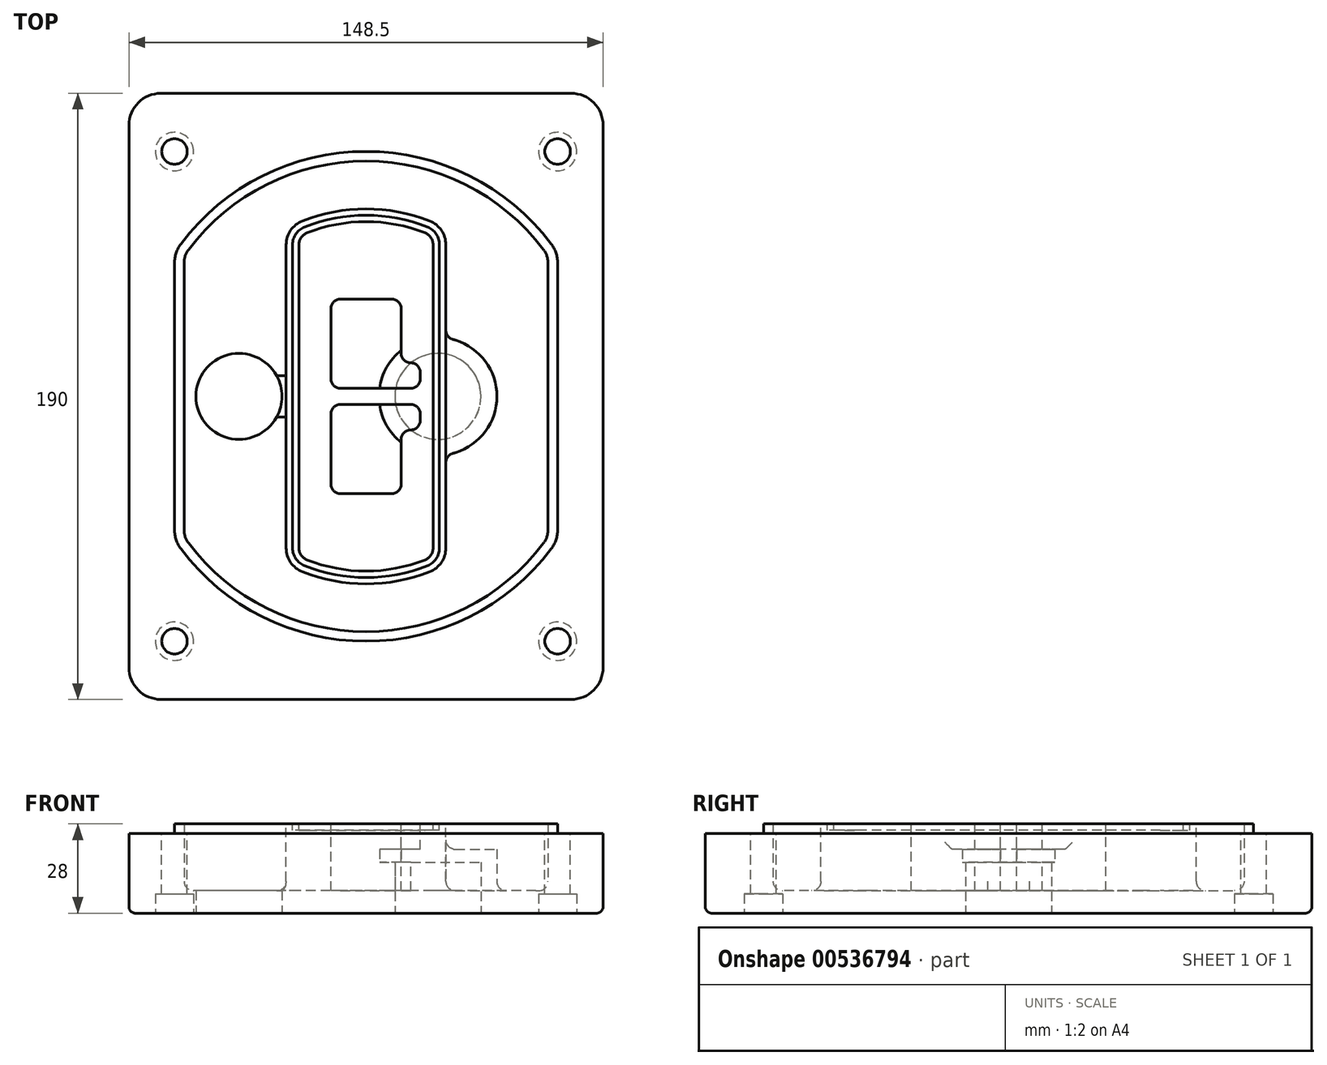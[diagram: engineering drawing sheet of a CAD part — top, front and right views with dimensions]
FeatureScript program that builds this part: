
annotation { "Feature Type Name" : "Feature", "Feature Type Description" : "" }
export const myFeature = defineFeature(function(context is Context, id is Id, definition is map)
    precondition{}
    {
        {
            var Q0;
            Q0=qCreatedBy(makeId("Top.planeOp"),FACE);
            var sketch = newSketch(context, id + "F0", { "sketchPlane" : qUnion([Q0])});
            skPoint(sketch, "E0.rect.middle", {"position": v(0, 0) * mm});
            skLineSegment(sketch, "E1.bottom", {"start": v(-64.25, -95) * mm, "end": v(64.25, -95) * mm});
            skLineSegment(sketch, "E1.top", {"start": v(-64.25, 95) * mm, "end": v(64.25, 95) * mm});
            skLineSegment(sketch, "E1.left", {"start": v(-74.25, -85) * mm, "end": v(-74.25, 85) * mm});
            skLineSegment(sketch, "E1.right", {"start": v(74.25, -85) * mm, "end": v(74.25, 85) * mm});
            skLineSegment(sketch, "E2", {"start": v(-74.25, 95) * mm, "end": v(74.25, -95) * mm, "construction": true});
            skLineSegment(sketch, "E3", {"start": v(74.25, 95) * mm, "end": v(-74.25, -95) * mm, "construction": true});
            skCircle(sketch, "E4", {"center": v(-60, 76.77) * mm, "radius": 4 * mm});
            skCircle(sketch, "E5", {"center": v(60, 76.77) * mm, "radius": 4 * mm});
            skCircle(sketch, "E6", {"center": v(60, -76.77) * mm, "radius": 4 * mm});
            skCircle(sketch, "E7", {"center": v(-60, -76.77) * mm, "radius": 4 * mm});
            skLineSegment(sketch, "E8", {"start": v(-60, 76.77) * mm, "end": v(60, 76.77) * mm, "construction": true});
            skLineSegment(sketch, "E9", {"start": v(60, 76.77) * mm, "end": v(60, -76.77) * mm, "construction": true});
            skLineSegment(sketch, "E10", {"start": v(60, -76.77) * mm, "end": v(-60, -76.77) * mm, "construction": true});
            skLineSegment(sketch, "E11", {"start": v(-60, -76.77) * mm, "end": v(-60, 76.77) * mm, "construction": true});
            skLineSegment(sketch, "E12", {"start": v(-60, 41.8) * mm, "end": v(-60, -41.8) * mm});
            skLineSegment(sketch, "E13", {"start": v(60, 41.8) * mm, "end": v(60, -41.8) * mm});
            skArc(sketch, "E14", {"start": v(58, 47.8) * mm, "mid": v(0, 76.77) * mm, "end": v(-58, 47.8) * mm});
            skArc(sketch, "E15", {"start": v(-58, -47.8) * mm, "mid": v(0, -76.77) * mm, "end": v(58, -47.8) * mm});
            skLineSegment(sketch, "E16", {"start": v(-60, 0) * mm, "end": v(60, 0) * mm, "construction": true});
            skPoint(sketch, "E17.visualSharp", {"position": v(-60, -45) * mm});
            skArc(sketch, "E17.filletArc", {"start": v(-60, -41.8) * mm, "mid": v(-59.49, -44.96) * mm, "end": v(-58, -47.8) * mm});
            skPoint(sketch, "E18.visualSharp", {"position": v(-60, 45) * mm});
            skArc(sketch, "E18.filletArc", {"start": v(-58, 47.8) * mm, "mid": v(-59.49, 44.96) * mm, "end": v(-60, 41.8) * mm});
            skPoint(sketch, "E19.visualSharp", {"position": v(60, 45) * mm});
            skArc(sketch, "E19.filletArc", {"start": v(60, 41.8) * mm, "mid": v(59.49, 44.96) * mm, "end": v(58, 47.8) * mm});
            skPoint(sketch, "E20.visualSharp", {"position": v(60, -45) * mm});
            skArc(sketch, "E20.filletArc", {"start": v(58, -47.8) * mm, "mid": v(59.49, -44.96) * mm, "end": v(60, -41.8) * mm});
            skPoint(sketch, "E21.visualSharp", {"position": v(-74.25, 95) * mm});
            skArc(sketch, "E21.filletArc", {"start": v(-64.25, 95) * mm, "mid": v(-71.32, 92.07) * mm, "end": v(-74.25, 85) * mm});
            skPoint(sketch, "E22.visualSharp", {"position": v(74.25, 95) * mm});
            skArc(sketch, "E22.filletArc", {"start": v(74.25, 85) * mm, "mid": v(71.32, 92.07) * mm, "end": v(64.25, 95) * mm});
            skPoint(sketch, "E23.visualSharp", {"position": v(74.25, -95) * mm});
            skArc(sketch, "E23.filletArc", {"start": v(64.25, -95) * mm, "mid": v(71.32, -92.07) * mm, "end": v(74.25, -85) * mm});
            skPoint(sketch, "E24.visualSharp", {"position": v(-74.25, -95) * mm});
            skArc(sketch, "E24.filletArc", {"start": v(-74.25, -85) * mm, "mid": v(-71.32, -92.07) * mm, "end": v(-64.25, -95) * mm});
            skArc(sketch, "E25.0", {"start": v(57, 41.8) * mm, "mid": v(56.64, 44.01) * mm, "end": v(55.6, 46) * mm});
            skLineSegment(sketch, "E25.1", {"start": v(57, 41.8) * mm, "end": v(57, -41.8) * mm});
            skArc(sketch, "E25.2", {"start": v(55.6, -46) * mm, "mid": v(56.64, -44.01) * mm, "end": v(57, -41.8) * mm});
            skArc(sketch, "E25.3", {"start": v(-55.6, -46) * mm, "mid": v(0, -73.77) * mm, "end": v(55.6, -46) * mm});
            skArc(sketch, "E25.4", {"start": v(-57, -41.8) * mm, "mid": v(-56.64, -44.01) * mm, "end": v(-55.6, -46) * mm});
            skArc(sketch, "E25.5", {"start": v(55.6, 46) * mm, "mid": v(0, 73.77) * mm, "end": v(-55.6, 46) * mm});
            skLineSegment(sketch, "E25.6", {"start": v(-57, 41.8) * mm, "end": v(-57, -41.8) * mm});
            skArc(sketch, "E25.7", {"start": v(-55.6, 46) * mm, "mid": v(-56.64, 44.01) * mm, "end": v(-57, 41.8) * mm});
            skArc(sketch, "E26.0", {"start": v(-61.2, 50.2) * mm, "mid": v(-63.28, 46.23) * mm, "end": v(-64, 41.8) * mm});
            skArc(sketch, "E26.1", {"start": v(61.2, 50.2) * mm, "mid": v(0, 80.77) * mm, "end": v(-61.2, 50.2) * mm});
            skArc(sketch, "E26.2", {"start": v(64, 41.8) * mm, "mid": v(63.28, 46.23) * mm, "end": v(61.2, 50.2) * mm});
            skLineSegment(sketch, "E26.3", {"start": v(64, 41.8) * mm, "end": v(64, -41.8) * mm});
            skArc(sketch, "E26.4", {"start": v(61.2, -50.2) * mm, "mid": v(63.28, -46.23) * mm, "end": v(64, -41.8) * mm});
            skLineSegment(sketch, "E26.5", {"start": v(-64, 41.8) * mm, "end": v(-64, -41.8) * mm});
            skArc(sketch, "E26.6", {"start": v(-61.2, -50.2) * mm, "mid": v(0, -80.77) * mm, "end": v(61.2, -50.2) * mm});
            skArc(sketch, "E26.7", {"start": v(-64, -41.8) * mm, "mid": v(-63.28, -46.23) * mm, "end": v(-61.2, -50.2) * mm});
            skSolve(sketch);
        }
        {
            var Q0;
            Q0=makeQuery(id+"F0.imprint","IMPRINT",FACE,{"disambiguationData":[TD([[makeQuery(id+"F0.imprint","IMPRINT",EDGE,{"derivedFrom":sQuery(id+"F0.wireOp",EDGE,"E1.bottom")}),1.0]])]});
            var Q1;
            Q1=makeQuery(id+"F0.imprint","IMPRINT",FACE,{"disambiguationData":[TD([[makeQuery(id+"F0.imprint","IMPRINT",EDGE,{"derivedFrom":sQuery(id+"F0.wireOp",EDGE,"E12")}),1.0]])]});
            var Q2;
            Q2=makeQuery(id+"F0.imprint","IMPRINT",FACE,{"disambiguationData":[TD([[makeQuery(id+"F0.imprint","IMPRINT",EDGE,{"derivedFrom":sQuery(id+"F0.wireOp",EDGE,"E25.0")}),1.0]])]});
            var Q3;
            Q3=makeQuery(id+"F0.imprint","IMPRINT",FACE,{"disambiguationData":[TD([[makeQuery(id+"F0.imprint","IMPRINT",EDGE,{"derivedFrom":sQuery(id+"F0.wireOp",EDGE,"E12")}),-1.0]])]});
            extrude(context, id + "F1", {"entities" : qUnion([Q0, Q1, Q2, Q3]), "oppositeDirection" : true, "depth" : 25 * mm, "offsetDistance" : 25 * mm});
        }
        {
            var Q0;
            Q0=makeQuery(id+"F0.imprint","IMPRINT",FACE,{"disambiguationData":[TD([[makeQuery(id+"F0.imprint","IMPRINT",EDGE,{"derivedFrom":sQuery(id+"F0.wireOp",EDGE,"E12")}),1.0]])]});
            extrude(context, id + "F2", {"entities" : qUnion([Q0]), "operationType" : NewBodyOperationType.ADD, "depth" : 3 * mm});
        }
        {
            var Q0;
            Q0=makeQuery(id+"F0.imprint","IMPRINT",FACE,{"disambiguationData":[TD([[makeQuery(id+"F0.imprint","IMPRINT",EDGE,{"derivedFrom":sQuery(id+"F0.wireOp",EDGE,"E25.0")}),1.0]])]});
            extrude(context, id + "F3", {"entities" : qUnion([Q0]), "operationType" : NewBodyOperationType.REMOVE, "oppositeDirection" : true, "depth" : 18 * mm});
        }
        {
            var Q0;
            Q0=makeQuery(id+"F2.opExtrude","CAP_FACE",FACE,{"disambiguationData":[OSD([sQuery(id+"F0.wireOp",EDGE,"E12"),sQuery(id+"F0.wireOp",EDGE,"E13"),sQuery(id+"F0.wireOp",EDGE,"E14"),sQuery(id+"F0.wireOp",EDGE,"E15"),sQuery(id+"F0.wireOp",EDGE,"E17.filletArc"),sQuery(id+"F0.wireOp",EDGE,"E18.filletArc"),sQuery(id+"F0.wireOp",EDGE,"E19.filletArc"),sQuery(id+"F0.wireOp",EDGE,"E20.filletArc"),sQuery(id+"F0.wireOp",EDGE,"E25.0"),sQuery(id+"F0.wireOp",EDGE,"E25.1"),sQuery(id+"F0.wireOp",EDGE,"E25.2"),sQuery(id+"F0.wireOp",EDGE,"E25.3"),sQuery(id+"F0.wireOp",EDGE,"E25.4"),sQuery(id+"F0.wireOp",EDGE,"E25.5"),sQuery(id+"F0.wireOp",EDGE,"E25.6"),sQuery(id+"F0.wireOp",EDGE,"E25.7")])],"isStart":false});
            var sketch = newSketch(context, id + "F4", { "sketchPlane" : qUnion([Q0])});
            skArc(sketch, "E27.0", {"start": v(-19.92, -55) * mm, "mid": v(0, -58.77) * mm, "end": v(19.92, -55) * mm});
            skArc(sketch, "E28.0", {"start": v(19.92, 55) * mm, "mid": v(0, 58.77) * mm, "end": v(-19.92, 55) * mm});
            skLineSegment(sketch, "E29", {"start": v(-25, 47.55) * mm, "end": v(-25, -47.55) * mm});
            skLineSegment(sketch, "E30", {"start": v(25, 47.55) * mm, "end": v(25, -47.55) * mm});
            skLineSegment(sketch, "E31", {"start": v(-25, 52.7) * mm, "end": v(25, 52.7) * mm, "construction": true});
            skLineSegment(sketch, "E32", {"start": v(-25, -52.7) * mm, "end": v(25, -52.7) * mm, "construction": true});
            skPoint(sketch, "E33.visualSharp", {"position": v(-25, 52.7) * mm});
            skArc(sketch, "E33.filletArc", {"start": v(-19.92, 55) * mm, "mid": v(-23.6, 52.06) * mm, "end": v(-25, 47.55) * mm});
            skPoint(sketch, "E34.visualSharp", {"position": v(25, 52.7) * mm});
            skArc(sketch, "E34.filletArc", {"start": v(25, 47.55) * mm, "mid": v(23.6, 52.06) * mm, "end": v(19.92, 55) * mm});
            skPoint(sketch, "E35.visualSharp", {"position": v(25, -52.7) * mm});
            skArc(sketch, "E35.filletArc", {"start": v(19.92, -55) * mm, "mid": v(23.6, -52.06) * mm, "end": v(25, -47.55) * mm});
            skPoint(sketch, "E36.visualSharp", {"position": v(-25, -52.7) * mm});
            skArc(sketch, "E36.filletArc", {"start": v(-25, -47.55) * mm, "mid": v(-23.6, -52.06) * mm, "end": v(-19.92, -55) * mm});
            skArc(sketch, "E37.0", {"start": v(55.6, 46) * mm, "mid": v(0, 73.77) * mm, "end": v(-55.6, 46) * mm});
            skArc(sketch, "E37.1", {"start": v(-55.6, 46) * mm, "mid": v(-56.64, 44.01) * mm, "end": v(-57, 41.8) * mm});
            skLineSegment(sketch, "E37.2", {"start": v(-57, 41.8) * mm, "end": v(-57, -41.8) * mm});
            skArc(sketch, "E37.3", {"start": v(-57, -41.8) * mm, "mid": v(-56.64, -44.01) * mm, "end": v(-55.6, -46) * mm});
            skArc(sketch, "E37.4", {"start": v(-55.6, -46) * mm, "mid": v(0, -73.77) * mm, "end": v(55.6, -46) * mm});
            skArc(sketch, "E37.5", {"start": v(55.6, -46) * mm, "mid": v(56.64, -44.01) * mm, "end": v(57, -41.8) * mm});
            skLineSegment(sketch, "E37.6", {"start": v(57, 41.8) * mm, "end": v(57, -41.8) * mm});
            skArc(sketch, "E37.7", {"start": v(57, 41.8) * mm, "mid": v(56.64, 44.01) * mm, "end": v(55.6, 46) * mm});
            skLineSegment(sketch, "E38.0", {"start": v(23, 47.55) * mm, "end": v(23, -47.55) * mm});
            skArc(sketch, "E38.1", {"start": v(19.2, -53.14) * mm, "mid": v(21.96, -50.93) * mm, "end": v(23, -47.55) * mm});
            skArc(sketch, "E38.2", {"start": v(-19.2, -53.14) * mm, "mid": v(0, -56.77) * mm, "end": v(19.2, -53.14) * mm});
            skArc(sketch, "E38.3", {"start": v(-23, -47.55) * mm, "mid": v(-21.96, -50.93) * mm, "end": v(-19.2, -53.14) * mm});
            skLineSegment(sketch, "E38.4", {"start": v(-23, 47.55) * mm, "end": v(-23, -47.55) * mm});
            skArc(sketch, "E38.5", {"start": v(23, 47.55) * mm, "mid": v(21.96, 50.93) * mm, "end": v(19.2, 53.14) * mm});
            skArc(sketch, "E38.6", {"start": v(-19.2, 53.14) * mm, "mid": v(-21.96, 50.93) * mm, "end": v(-23, 47.55) * mm});
            skArc(sketch, "E38.7", {"start": v(19.2, 53.14) * mm, "mid": v(0, 56.77) * mm, "end": v(-19.2, 53.14) * mm});
            skArc(sketch, "E39.0", {"start": v(21, 47.55) * mm, "mid": v(20.3, 49.8) * mm, "end": v(18.46, 51.28) * mm});
            skLineSegment(sketch, "E39.1", {"start": v(21, 47.55) * mm, "end": v(21, -47.55) * mm});
            skArc(sketch, "E39.2", {"start": v(18.46, -51.28) * mm, "mid": v(20.3, -49.8) * mm, "end": v(21, -47.55) * mm});
            skArc(sketch, "E39.3", {"start": v(-18.46, -51.28) * mm, "mid": v(0, -54.77) * mm, "end": v(18.46, -51.28) * mm});
            skArc(sketch, "E39.4", {"start": v(-21, -47.55) * mm, "mid": v(-20.3, -49.8) * mm, "end": v(-18.46, -51.28) * mm});
            skArc(sketch, "E39.5", {"start": v(18.46, 51.28) * mm, "mid": v(0, 54.77) * mm, "end": v(-18.46, 51.28) * mm});
            skLineSegment(sketch, "E39.6", {"start": v(-21, 47.55) * mm, "end": v(-21, -47.55) * mm});
            skArc(sketch, "E39.7", {"start": v(-18.46, 51.28) * mm, "mid": v(-20.3, 49.8) * mm, "end": v(-21, 47.55) * mm});
            skLineSegment(sketch, "E40", {"start": v(-25, 0) * mm, "end": v(25, 0) * mm, "construction": true});
            skLineSegment(sketch, "E41", {"start": v(-11, 5.5) * mm, "end": v(-11, 27.5) * mm});
            skLineSegment(sketch, "E42", {"start": v(-8, 30.5) * mm, "end": v(8, 30.5) * mm});
            skLineSegment(sketch, "E43", {"start": v(11, 27.5) * mm, "end": v(11, 13.5) * mm});
            skLineSegment(sketch, "E44", {"start": v(14, 10.5) * mm, "end": v(14, 10.5) * mm});
            skLineSegment(sketch, "E45", {"start": v(17, 7.5) * mm, "end": v(17, 5.5) * mm});
            skLineSegment(sketch, "E46", {"start": v(14, 2.5) * mm, "end": v(-8, 2.5) * mm});
            skPoint(sketch, "E47.visualSharp", {"position": v(-11, 30.5) * mm});
            skArc(sketch, "E47.filletArc", {"start": v(-8, 30.5) * mm, "mid": v(-10.12, 29.62) * mm, "end": v(-11, 27.5) * mm});
            skPoint(sketch, "E48.visualSharp", {"position": v(11, 30.5) * mm});
            skArc(sketch, "E48.filletArc", {"start": v(11, 27.5) * mm, "mid": v(10.12, 29.62) * mm, "end": v(8, 30.5) * mm});
            skPoint(sketch, "E49.visualSharp", {"position": v(11, 10.5) * mm});
            skArc(sketch, "E49.filletArc", {"start": v(11, 13.5) * mm, "mid": v(11.88, 11.38) * mm, "end": v(14, 10.5) * mm});
            skPoint(sketch, "E50.visualSharp", {"position": v(17, 10.5) * mm});
            skArc(sketch, "E50.filletArc", {"start": v(17, 7.5) * mm, "mid": v(16.12, 9.62) * mm, "end": v(14, 10.5) * mm});
            skPoint(sketch, "E51.visualSharp", {"position": v(17, 2.5) * mm});
            skArc(sketch, "E51.filletArc", {"start": v(14, 2.5) * mm, "mid": v(16.12, 3.38) * mm, "end": v(17, 5.5) * mm});
            skPoint(sketch, "E52.visualSharp", {"position": v(-11, 2.5) * mm});
            skArc(sketch, "E52.filletArc", {"start": v(-11, 5.5) * mm, "mid": v(-10.12, 3.38) * mm, "end": v(-8, 2.5) * mm});
            skLineSegment(sketch, "E53.0.MirrorCS", {"start": v(14, -2.5) * mm, "end": v(-8, -2.5) * mm});
            skArc(sketch, "E54.0.MirrorCS", {"start": v(-11, -5.5) * mm, "mid": v(-10.12, -3.38) * mm, "end": v(-8, -2.5) * mm});
            skLineSegment(sketch, "E55.0.MirrorCS", {"start": v(-11, -5.5) * mm, "end": v(-11, -27.5) * mm});
            skArc(sketch, "E56.0.MirrorCS", {"start": v(-8, -30.5) * mm, "mid": v(-10.12, -29.62) * mm, "end": v(-11, -27.5) * mm});
            skLineSegment(sketch, "E57.0.MirrorCS", {"start": v(-8, -30.5) * mm, "end": v(8, -30.5) * mm});
            skArc(sketch, "E58.0.MirrorCS", {"start": v(11, -27.5) * mm, "mid": v(10.12, -29.62) * mm, "end": v(8, -30.5) * mm});
            skLineSegment(sketch, "E59.0.MirrorCS", {"start": v(11, -27.5) * mm, "end": v(11, -13.5) * mm});
            skArc(sketch, "E60.0.MirrorCS", {"start": v(11, -13.5) * mm, "mid": v(11.88, -11.38) * mm, "end": v(14, -10.5) * mm});
            skArc(sketch, "E61.0.MirrorCS", {"start": v(17, -7.5) * mm, "mid": v(16.12, -9.62) * mm, "end": v(14, -10.5) * mm});
            skLineSegment(sketch, "E62.0.MirrorCS", {"start": v(17, -7.5) * mm, "end": v(17, -5.5) * mm});
            skArc(sketch, "E63.0.MirrorCS", {"start": v(14, -2.5) * mm, "mid": v(16.12, -3.38) * mm, "end": v(17, -5.5) * mm});
            skSolve(sketch);
        }
        {
            var Q0;
            Q0=makeQuery(id+"F4.imprint","IMPRINT",FACE,{"disambiguationData":[TD([[makeQuery(id+"F4.imprint","IMPRINT",EDGE,{"derivedFrom":sQuery(id+"F4.wireOp",EDGE,"E27.0")}),1.0]])]});
            var Q1;
            Q1=makeQuery(id+"F4.imprint","IMPRINT",FACE,{"disambiguationData":[TD([[makeQuery(id+"F4.imprint","IMPRINT",EDGE,{"derivedFrom":sQuery(id+"F4.wireOp",EDGE,"E38.0")}),-1.0]])]});
            var Q2;
            Q2=makeQuery(id+"F4.imprint","IMPRINT",FACE,{"disambiguationData":[TD([[makeQuery(id+"F4.imprint","IMPRINT",EDGE,{"derivedFrom":sQuery(id+"F4.wireOp",EDGE,"E39.0")}),1.0]])]});
            extrude(context, id + "F5", {"entities" : qUnion([Q0, Q1, Q2]), "operationType" : NewBodyOperationType.ADD, "endBound" : BoundingType.UP_TO_NEXT, "oppositeDirection" : true, "depth" : 25 * mm});
        }
        {
            var Q0;
            Q0=makeQuery(id+"F4.imprint","IMPRINT",FACE,{"disambiguationData":[TD([[makeQuery(id+"F4.imprint","IMPRINT",EDGE,{"derivedFrom":sQuery(id+"F4.wireOp",EDGE,"E38.0")}),-1.0]])]});
            extrude(context, id + "F6", {"entities" : qUnion([Q0]), "operationType" : NewBodyOperationType.REMOVE, "oppositeDirection" : true, "depth" : 2 * mm});
        }
        {
            var Q0;
            Q0=makeQuery(id+"F1.opExtrude","CAP_FACE",FACE,{"disambiguationData":[OSD([sQuery(id+"F0.wireOp",EDGE,"E1.bottom"),sQuery(id+"F0.wireOp",EDGE,"E1.top"),sQuery(id+"F0.wireOp",EDGE,"E1.left"),sQuery(id+"F0.wireOp",EDGE,"E1.right"),sQuery(id+"F0.wireOp",EDGE,"E4"),sQuery(id+"F0.wireOp",EDGE,"E5"),sQuery(id+"F0.wireOp",EDGE,"E6"),sQuery(id+"F0.wireOp",EDGE,"E7"),sQuery(id+"F0.wireOp",EDGE,"E21.filletArc"),sQuery(id+"F0.wireOp",EDGE,"E22.filletArc"),sQuery(id+"F0.wireOp",EDGE,"E23.filletArc"),sQuery(id+"F0.wireOp",EDGE,"E24.filletArc")])],"isStart":false});
            var sketch = newSketch(context, id + "F7", { "sketchPlane" : qUnion([Q0])});
            skCircle(sketch, "E64", {"center": v(22.5, 0) * mm, "radius": 13.47 * mm});
            skCircle(sketch, "E65", {"center": v(-39.81, 0) * mm, "radius": 13.47 * mm});
            skLineSegment(sketch, "E66", {"start": v(74.25, 0) * mm, "end": v(-74.25, 0) * mm});
            skCircle(sketch, "E67", {"center": v(22.5, 0) * mm, "radius": 18.47 * mm});
            skCircle(sketch, "E68", {"center": v(60, -76.77) * mm, "radius": 6 * mm});
            skCircle(sketch, "E69", {"center": v(-60, -76.77) * mm, "radius": 6 * mm});
            skCircle(sketch, "E70", {"center": v(-60, 76.77) * mm, "radius": 6 * mm});
            skCircle(sketch, "E71", {"center": v(60, 76.77) * mm, "radius": 6 * mm});
            skSolve(sketch);
        }
        {
            var Q0;
            {var subQ1=sQuery(id+"F7.wireOp",EDGE,"E66");var subQ4=sQuery(id+"F7.wireOp",EDGE,"E64");var subQ6=makeQuery(id+"F7.imprint","INTERSECT",VERTEX,{"disambiguationData":[OD(0.0)],"derivedFrom":[subQ4,subQ1]});Q0=makeQuery(id+"F7.imprint","IMPRINT",FACE,{"disambiguationData":[TD([[makeQuery(id+"F7.imprint","IMPRINT",EDGE,{"disambiguationData":[TD([[subQ6,-1.0]])],"derivedFrom":subQ4}),-1.0]])]});}
            var Q1;
            {var subQ0=sQuery(id+"F7.wireOp",EDGE,"E66");var subQ1=sQuery(id+"F7.wireOp",EDGE,"E64");var subQ3=makeQuery(id+"F7.imprint","INTERSECT",VERTEX,{"disambiguationData":[OD(0.0)],"derivedFrom":[subQ1,subQ0]});Q1=makeQuery(id+"F7.imprint","IMPRINT",FACE,{"disambiguationData":[TD([[makeQuery(id+"F7.imprint","IMPRINT",EDGE,{"disambiguationData":[TD([[subQ3,-1.0]])],"derivedFrom":subQ1}),1.0]])]});}
            var Q2;
            {var subQ0=sQuery(id+"F7.wireOp",EDGE,"E66");var subQ1=sQuery(id+"F7.wireOp",EDGE,"E64");var subQ3=makeQuery(id+"F7.imprint","INTERSECT",VERTEX,{"disambiguationData":[OD(0.0)],"derivedFrom":[subQ1,subQ0]});Q2=makeQuery(id+"F7.imprint","IMPRINT",FACE,{"disambiguationData":[TD([[makeQuery(id+"F7.imprint","IMPRINT",EDGE,{"disambiguationData":[TD([[subQ3,1.0]])],"derivedFrom":subQ1}),1.0]])]});}
            var Q3;
            {var subQ1=sQuery(id+"F7.wireOp",EDGE,"E66");var subQ4=sQuery(id+"F7.wireOp",EDGE,"E64");var subQ6=makeQuery(id+"F7.imprint","INTERSECT",VERTEX,{"disambiguationData":[OD(0.0)],"derivedFrom":[subQ4,subQ1]});Q3=makeQuery(id+"F7.imprint","IMPRINT",FACE,{"disambiguationData":[TD([[makeQuery(id+"F7.imprint","IMPRINT",EDGE,{"disambiguationData":[TD([[subQ6,1.0]])],"derivedFrom":subQ4}),-1.0]])]});}
            extrude(context, id + "F8", {"entities" : qUnion([Q0, Q1, Q2, Q3]), "operationType" : NewBodyOperationType.ADD, "oppositeDirection" : true, "depth" : 20 * mm});
        }
        {
            var Q0;
            {var subQ0=sQuery(id+"F7.wireOp",EDGE,"E66");var subQ1=sQuery(id+"F7.wireOp",EDGE,"E64");var subQ3=makeQuery(id+"F7.imprint","INTERSECT",VERTEX,{"disambiguationData":[OD(0.0)],"derivedFrom":[subQ1,subQ0]});Q0=makeQuery(id+"F7.imprint","IMPRINT",FACE,{"disambiguationData":[TD([[makeQuery(id+"F7.imprint","IMPRINT",EDGE,{"disambiguationData":[TD([[subQ3,-1.0]])],"derivedFrom":subQ1}),1.0]])]});}
            var Q1;
            {var subQ0=sQuery(id+"F7.wireOp",EDGE,"E66");var subQ1=sQuery(id+"F7.wireOp",EDGE,"E64");var subQ3=makeQuery(id+"F7.imprint","INTERSECT",VERTEX,{"disambiguationData":[OD(0.0)],"derivedFrom":[subQ1,subQ0]});Q1=makeQuery(id+"F7.imprint","IMPRINT",FACE,{"disambiguationData":[TD([[makeQuery(id+"F7.imprint","IMPRINT",EDGE,{"disambiguationData":[TD([[subQ3,1.0]])],"derivedFrom":subQ1}),1.0]])]});}
            extrude(context, id + "F9", {"entities" : qUnion([Q0, Q1]), "operationType" : NewBodyOperationType.REMOVE, "oppositeDirection" : true, "depth" : 16 * mm});
        }
        {
            var Q0;
            {var subQ0=sQuery(id+"F7.wireOp",EDGE,"E66");var subQ1=sQuery(id+"F7.wireOp",EDGE,"E65");var subQ3=makeQuery(id+"F7.imprint","INTERSECT",VERTEX,{"disambiguationData":[OD(0.0)],"derivedFrom":[subQ1,subQ0]});Q0=makeQuery(id+"F7.imprint","IMPRINT",FACE,{"disambiguationData":[TD([[makeQuery(id+"F7.imprint","IMPRINT",EDGE,{"disambiguationData":[TD([[subQ3,-1.0]])],"derivedFrom":subQ1}),1.0]])]});}
            var Q1;
            {var subQ0=sQuery(id+"F7.wireOp",EDGE,"E66");var subQ1=sQuery(id+"F7.wireOp",EDGE,"E65");var subQ3=makeQuery(id+"F7.imprint","INTERSECT",VERTEX,{"disambiguationData":[OD(0.0)],"derivedFrom":[subQ1,subQ0]});Q1=makeQuery(id+"F7.imprint","IMPRINT",FACE,{"disambiguationData":[TD([[makeQuery(id+"F7.imprint","IMPRINT",EDGE,{"disambiguationData":[TD([[subQ3,1.0]])],"derivedFrom":subQ1}),1.0]])]});}
            extrude(context, id + "F10", {"entities" : qUnion([Q0, Q1]), "operationType" : NewBodyOperationType.REMOVE, "oppositeDirection" : true, "depth" : 25 * mm});
        }
        {
            var Q0;
            Q0=makeQuery(id+"F7.imprint","IMPRINT",FACE,{"disambiguationData":[TD([[makeQuery(id+"F7.imprint","IMPRINT",EDGE,{"derivedFrom":sQuery(id+"F7.wireOp",EDGE,"E68")}),1.0]])]});
            var Q1;
            Q1=makeQuery(id+"F7.imprint","IMPRINT",FACE,{"disambiguationData":[TD([[makeQuery(id+"F7.imprint","IMPRINT",EDGE,{"derivedFrom":makeQuery(id+"F1.opExtrude","CAP_EDGE",EDGE,{"disambiguationData":[OSD([sQuery(id+"F0.wireOp",EDGE,"E5")])],"isStart":false})}),-1.0]])]});
            var Q2;
            Q2=makeQuery(id+"F7.imprint","IMPRINT",FACE,{"disambiguationData":[TD([[makeQuery(id+"F7.imprint","IMPRINT",EDGE,{"derivedFrom":sQuery(id+"F7.wireOp",EDGE,"E69")}),1.0]])]});
            var Q3;
            Q3=makeQuery(id+"F7.imprint","IMPRINT",FACE,{"disambiguationData":[TD([[makeQuery(id+"F7.imprint","IMPRINT",EDGE,{"derivedFrom":makeQuery(id+"F1.opExtrude","CAP_EDGE",EDGE,{"disambiguationData":[OSD([sQuery(id+"F0.wireOp",EDGE,"E4")])],"isStart":false})}),-1.0]])]});
            var Q4;
            Q4=makeQuery(id+"F7.imprint","IMPRINT",FACE,{"disambiguationData":[TD([[makeQuery(id+"F7.imprint","IMPRINT",EDGE,{"derivedFrom":sQuery(id+"F7.wireOp",EDGE,"E70")}),1.0]])]});
            var Q5;
            Q5=makeQuery(id+"F7.imprint","IMPRINT",FACE,{"disambiguationData":[TD([[makeQuery(id+"F7.imprint","IMPRINT",EDGE,{"derivedFrom":makeQuery(id+"F1.opExtrude","CAP_EDGE",EDGE,{"disambiguationData":[OSD([sQuery(id+"F0.wireOp",EDGE,"E7")])],"isStart":false})}),-1.0]])]});
            var Q6;
            Q6=makeQuery(id+"F7.imprint","IMPRINT",FACE,{"disambiguationData":[TD([[makeQuery(id+"F7.imprint","IMPRINT",EDGE,{"derivedFrom":sQuery(id+"F7.wireOp",EDGE,"E71")}),1.0]])]});
            var Q7;
            Q7=makeQuery(id+"F7.imprint","IMPRINT",FACE,{"disambiguationData":[TD([[makeQuery(id+"F7.imprint","IMPRINT",EDGE,{"derivedFrom":makeQuery(id+"F1.opExtrude","CAP_EDGE",EDGE,{"disambiguationData":[OSD([sQuery(id+"F0.wireOp",EDGE,"E6")])],"isStart":false})}),-1.0]])]});
            extrude(context, id + "F11", {"entities" : qUnion([Q0, Q1, Q2, Q3, Q4, Q5, Q6, Q7]), "operationType" : NewBodyOperationType.REMOVE, "oppositeDirection" : true, "depth" : 6 * mm});
        }
        {
            var Q0;
            Q0=makeQuery(id+"F9.boolean.opBoolean","COPY",FACE,{"derivedFrom":makeQuery(id+"F9.opExtrude","CAP_FACE",FACE,{"disambiguationData":[OSD([sQuery(id+"F7.wireOp",EDGE,"E64")])],"isStart":false})});
            var sketch = newSketch(context, id + "F12", { "sketchPlane" : qUnion([Q0])});
            skArc(sketch, "E72.0", {"start": v(11, 14.45) * mm, "mid": v(6.45, 9.13) * mm, "end": v(4.2, 2.5) * mm});
            skArc(sketch, "E72.1", {"start": v(4.2, -2.5) * mm, "mid": v(6.45, -9.13) * mm, "end": v(11, -14.45) * mm});
            skLineSegment(sketch, "E73", {"start": v(4.2, -2.5) * mm, "end": v(14, -2.5) * mm});
            skLineSegment(sketch, "E74.0", {"start": v(14, 2.5) * mm, "end": v(4.2, 2.5) * mm});
            skArc(sketch, "E74.1", {"start": v(14, 2.5) * mm, "mid": v(16.12, 3.38) * mm, "end": v(17, 5.5) * mm});
            skLineSegment(sketch, "E74.2", {"start": v(17, 7.5) * mm, "end": v(17, 5.5) * mm});
            skArc(sketch, "E74.3", {"start": v(17, 7.5) * mm, "mid": v(16.12, 9.62) * mm, "end": v(14, 10.5) * mm});
            skArc(sketch, "E74.4", {"start": v(11, 13.5) * mm, "mid": v(11.88, 11.38) * mm, "end": v(14, 10.5) * mm});
            skLineSegment(sketch, "E74.5", {"start": v(11, 14.45) * mm, "end": v(11, 13.5) * mm});
            skLineSegment(sketch, "E74.7", {"start": v(14, -2.5) * mm, "end": v(4.2, -2.5) * mm});
            skArc(sketch, "E74.8", {"start": v(14, -2.5) * mm, "mid": v(16.12, -3.38) * mm, "end": v(17, -5.5) * mm});
            skLineSegment(sketch, "E74.9", {"start": v(17, -7.5) * mm, "end": v(17, -5.5) * mm});
            skArc(sketch, "E74.10", {"start": v(17, -7.5) * mm, "mid": v(16.12, -9.62) * mm, "end": v(14, -10.5) * mm});
            skArc(sketch, "E74.11", {"start": v(11, -13.5) * mm, "mid": v(11.88, -11.38) * mm, "end": v(14, -10.5) * mm});
            skLineSegment(sketch, "E74.12", {"start": v(11, -14.45) * mm, "end": v(11, -13.5) * mm});
            skPoint(sketch, "E75.orphan", {"position": v(11, -27.5) * mm});
            skPoint(sketch, "E76.orphan", {"position": v(-8, -2.5) * mm});
            skPoint(sketch, "E77.orphan", {"position": v(-8, 2.5) * mm});
            skPoint(sketch, "E78.orphan", {"position": v(11, 27.5) * mm});
            skSolve(sketch);
        }
        {
            var Q0;
            {var subQ7=sQuery(id+"F12.wireOp",EDGE,"E72.0");var subQ14=sQuery(id+"F12.wireOp",EDGE,"E72.1");var subQ16=sQuery(id+"F12.wireOp",EDGE,"E74.1");var subQ18=sQuery(id+"F12.wireOp",EDGE,"E74.8");Q0=qUnion([makeQuery(id+"F12.imprint","IMPRINT",FACE,{"disambiguationData":[TD([[makeQuery(id+"F12.imprint","IMPRINT",EDGE,{"derivedFrom":subQ7}),1.0]])]}),makeQuery(id+"F12.imprint","IMPRINT",FACE,{"disambiguationData":[TD([[makeQuery(id+"F12.imprint","IMPRINT",EDGE,{"derivedFrom":subQ14}),1.0]])]}),makeQuery(id+"F12.imprint","IMPRINT",FACE,{"disambiguationData":[TD([[makeQuery(id+"F12.imprint","IMPRINT",EDGE,{"derivedFrom":subQ16}),1.0]])]}),makeQuery(id+"F12.imprint","IMPRINT",FACE,{"disambiguationData":[TD([[makeQuery(id+"F12.imprint","IMPRINT",EDGE,{"derivedFrom":subQ18}),-1.0]])]})]);}
            var Q1;
            Q1=makeQuery(id+"F5.boolean.opBoolean","SPLIT",FACE,{"disambiguationData":[TD([makeQuery(id+"F5.opExtrude","SWEPT_FACE",FACE,{"disambiguationData":[OSD([sQuery(id+"F4.wireOp",EDGE,"E41")])]})])],"derivedFrom":makeQuery(id+"F3.boolean.opBoolean","COPY",FACE,{"derivedFrom":makeQuery(id+"F3.opExtrude","CAP_FACE",FACE,{"disambiguationData":[OSD([sQuery(id+"F0.wireOp",EDGE,"E25.0"),sQuery(id+"F0.wireOp",EDGE,"E25.1"),sQuery(id+"F0.wireOp",EDGE,"E25.2"),sQuery(id+"F0.wireOp",EDGE,"E25.3"),sQuery(id+"F0.wireOp",EDGE,"E25.4"),sQuery(id+"F0.wireOp",EDGE,"E25.5"),sQuery(id+"F0.wireOp",EDGE,"E25.6"),sQuery(id+"F0.wireOp",EDGE,"E25.7")])],"isStart":false})})});
            extrude(context, id + "F13", {"entities" : qUnion([Q0]), "operationType" : NewBodyOperationType.REMOVE, "endBound" : BoundingType.UP_TO_SURFACE, "endBoundEntityFace" : qUnion([Q1]), "depth" : 25 * mm});
        }
        {
            var Q0;
            Q0=makeQuery(id+"F3.boolean.opBoolean","COPY",EDGE,{"derivedFrom":makeQuery(id+"F3.opExtrude","CAP_EDGE",EDGE,{"disambiguationData":[OSD([sQuery(id+"F0.wireOp",EDGE,"E25.6")])],"isStart":false})});
            var Q1;
            Q1=makeQuery(id+"F8.boolean.opBoolean","INTERSECT",EDGE,{"derivedFrom":[makeQuery(id+"F5.opExtrude","SWEPT_FACE",FACE,{"disambiguationData":[OSD([sQuery(id+"F4.wireOp",EDGE,"E30")])]}),makeQuery(id+"F8.opExtrude","CAP_FACE",FACE,{"disambiguationData":[OSD([sQuery(id+"F7.wireOp",EDGE,"E67")])],"isStart":false})]});
            var Q2;
            Q2=makeQuery(id+"F8.boolean.opBoolean","INTERSECT",EDGE,{"disambiguationData":[OD(1.0)],"derivedFrom":[makeQuery(id+"F5.opExtrude","SWEPT_FACE",FACE,{"disambiguationData":[OSD([sQuery(id+"F4.wireOp",EDGE,"E30")])]}),makeQuery(id+"F8.opExtrude","SWEPT_FACE",FACE,{"disambiguationData":[OSD([sQuery(id+"F7.wireOp",EDGE,"E67")])]})]});
            var Q3;
            {var subQ0=sQuery(id+"F4.wireOp",EDGE,"E30");Q3=makeQuery(id+"F8.boolean.opBoolean","SPLIT",EDGE,{"disambiguationData":[TD([makeQuery(id+"F5.opExtrude","SWEPT_FACE",FACE,{"disambiguationData":[OSD([sQuery(id+"F4.wireOp",EDGE,"E35.filletArc")])]})])],"derivedFrom":makeQuery(id+"F5.opExtrude","CAP_EDGE",EDGE,{"disambiguationData":[OSD([subQ0])],"isStart":false})});}
            var Q4;
            {var subQ0=sQuery(id+"F0.wireOp",EDGE,"E25.7");var subQ1=sQuery(id+"F0.wireOp",EDGE,"E25.1");var subQ2=sQuery(id+"F0.wireOp",EDGE,"E25.6");var subQ3=sQuery(id+"F0.wireOp",EDGE,"E25.5");var subQ4=sQuery(id+"F0.wireOp",EDGE,"E25.4");var subQ5=sQuery(id+"F0.wireOp",EDGE,"E25.0");var subQ6=sQuery(id+"F0.wireOp",EDGE,"E25.2");var subQ7=sQuery(id+"F0.wireOp",EDGE,"E25.3");Q4=makeQuery(id+"F8.boolean.opBoolean","INTERSECT",EDGE,{"derivedFrom":[makeQuery(id+"F5.boolean.opBoolean","SPLIT",FACE,{"disambiguationData":[TD([makeQuery(id+"F2.opExtrude","SWEPT_FACE",FACE,{"disambiguationData":[OSD([subQ5])]})])],"derivedFrom":makeQuery(id+"F3.boolean.opBoolean","COPY",FACE,{"derivedFrom":makeQuery(id+"F3.opExtrude","CAP_FACE",FACE,{"disambiguationData":[OSD([subQ5,subQ1,subQ6,subQ7,subQ4,subQ3,subQ2,subQ0])],"isStart":false})})}),makeQuery(id+"F8.opExtrude","SWEPT_FACE",FACE,{"disambiguationData":[OSD([sQuery(id+"F7.wireOp",EDGE,"E67")])]})]});}
            var Q5;
            Q5=makeQuery(id+"F8.boolean.opBoolean","INTERSECT",EDGE,{"disambiguationData":[OD(0.0)],"derivedFrom":[makeQuery(id+"F5.opExtrude","SWEPT_FACE",FACE,{"disambiguationData":[OSD([sQuery(id+"F4.wireOp",EDGE,"E30")])]}),makeQuery(id+"F8.opExtrude","SWEPT_FACE",FACE,{"disambiguationData":[OSD([sQuery(id+"F7.wireOp",EDGE,"E67")])]})]});
            fillet(context, id + "F14", {"entities" : qUnion([Q0, Q1, Q2, Q3, Q4, Q5]), "radius" : 3 * mm, "tangentPropagation" : true, "allowEdgeOverflow" : false});
        }
        {
            var Q0;
            Q0=makeQuery(id+"F1.opExtrude","CAP_EDGE",EDGE,{"disambiguationData":[OSD([sQuery(id+"F0.wireOp",EDGE,"E1.bottom")])],"isStart":false});
            fillet(context, id + "F15", {"entities" : qUnion([Q0]), "radius" : 2 * mm, "tangentPropagation" : true, "allowEdgeOverflow" : false});
        }
    });
